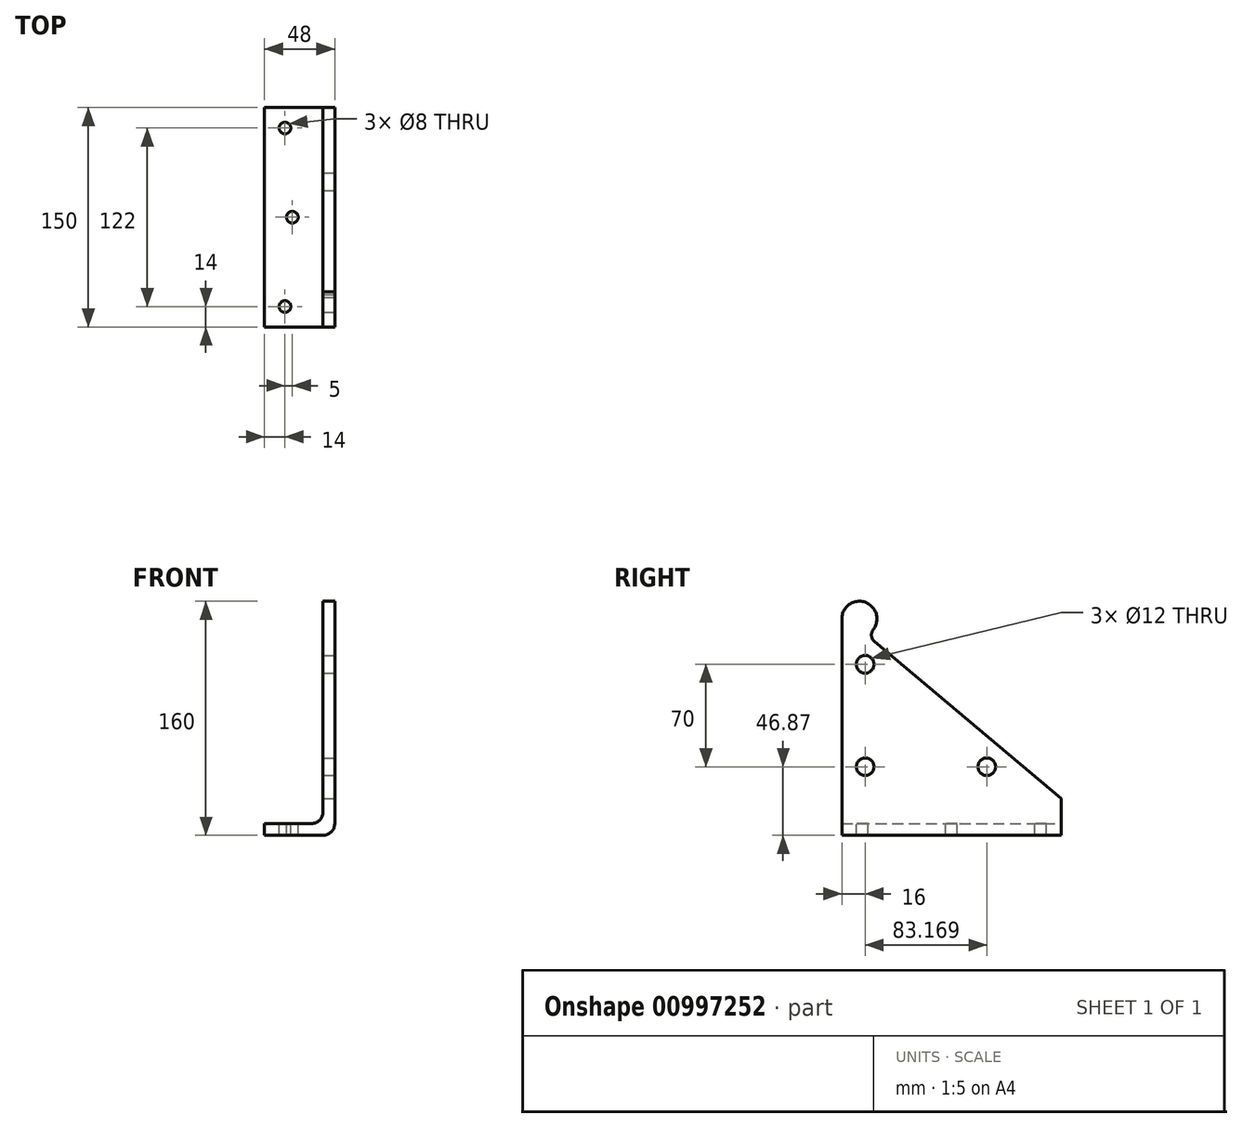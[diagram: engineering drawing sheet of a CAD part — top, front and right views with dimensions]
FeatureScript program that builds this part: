
annotation { "Feature Type Name" : "Feature", "Feature Type Description" : "" }
export const myFeature = defineFeature(function(context is Context, id is Id, definition is map)
    precondition{}
    {
        {
            var Q0;
            Q0=qCreatedBy(makeId("Front.planeOp"),FACE);
            var sketch = newSketch(context, id + "F0", { "sketchPlane" : qUnion([Q0])});
            skLineSegment(sketch, "E0", {"start": v(-4, 80) * mm, "end": v(-4, -72) * mm});
            skLineSegment(sketch, "E1", {"start": v(4, -80) * mm, "end": v(4, 80) * mm});
            skLineSegment(sketch, "E2", {"start": v(4, 80) * mm, "end": v(-4, 80) * mm});
            skLineSegment(sketch, "E3", {"start": v(4, -80) * mm, "end": v(-44, -80) * mm});
            skLineSegment(sketch, "E4", {"start": v(-44, -80) * mm, "end": v(-44, -72) * mm});
            skLineSegment(sketch, "E5", {"start": v(-44, -72) * mm, "end": v(-4, -72) * mm});
            skSolve(sketch);
        }
        {
            var Q0;
            Q0=qSketchRegion(id+"F0",true);
            extrude(context, id + "F1", {"entities" : qUnion([Q0]), "endBound" : BoundingType.SYMMETRIC, "depth" : 150 * mm, "offsetDistance" : 25 * mm});
        }
        {
            var Q0;
            Q0=makeQuery(id+"F1.opExtrude","SWEPT_EDGE",EDGE,{"disambiguationData":[OSD([sQuery(id+"F0.wireOp",EDGE,"E0"),sQuery(id+"F0.wireOp",EDGE,"E5")])]});
            var Q1;
            Q1=makeQuery(id+"F1.opExtrude","SWEPT_EDGE",EDGE,{"disambiguationData":[OSD([sQuery(id+"F0.wireOp",EDGE,"E1"),sQuery(id+"F0.wireOp",EDGE,"E3")])]});
            fillet(context, id + "F2", {"entities" : qUnion([Q0, Q1]), "radius" : 8 * mm, "tangentPropagation" : true, "allowEdgeOverflow" : false});
        }
        {
            var Q0;
            Q0=makeQuery(id+"F1.opExtrude","SWEPT_FACE",FACE,{"disambiguationData":[OSD([sQuery(id+"F0.wireOp",EDGE,"E1")])]});
            var sketch = newSketch(context, id + "F3", { "sketchPlane" : qUnion([Q0])});
            skCircle(sketch, "E6", {"center": v(-63, 68) * mm, "radius": 12 * mm});
            skArc(sketch, "E7", {"start": v(-53.5, 60.67) * mm, "mid": v(-54.72, 56.36) * mm, "end": v(-52.62, 52.4) * mm});
            skLineSegment(sketch, "E8", {"start": v(75, -55) * mm, "end": v(-52.62, 52.4) * mm});
            skLineSegment(sketch, "E9", {"start": v(-63, 80) * mm, "end": v(75, 80) * mm});
            skLineSegment(sketch, "E10", {"start": v(75, 80) * mm, "end": v(75, -55) * mm});
            skCircle(sketch, "E11", {"center": v(-59, 36.87) * mm, "radius": 6 * mm});
            skCircle(sketch, "E12", {"center": v(-59, -33.13) * mm, "radius": 6 * mm});
            skCircle(sketch, "E13", {"center": v(24.17, -33.13) * mm, "radius": 6 * mm});
            skSolve(sketch);
        }
        {
            var Q0;
            {var subQ1=sQuery(id+"F3.wireOp",EDGE,"E7");Q0=makeQuery(id+"F3.imprint","IMPRINT",FACE,{"disambiguationData":[TD([[makeQuery(id+"F3.imprint","IMPRINT",EDGE,{"derivedFrom":subQ1}),1.0]])]});}
            var Q1;
            {var subQ0=sQuery(id+"F3.wireOp",EDGE,"E6");var subQ1=sQuery(id+"F0.wireOp",EDGE,"E1");var subQ4=makeQuery(id+"F1.opExtrude","CAP_EDGE",EDGE,{"disambiguationData":[OSD([subQ1])],"isStart":false});var subQ5=makeQuery(id+"F3.imprint","INTERSECT",VERTEX,{"derivedFrom":[subQ4,subQ0]});Q1=makeQuery(id+"F3.imprint","IMPRINT",FACE,{"disambiguationData":[TD([[makeQuery(id+"F3.imprint","IMPRINT",EDGE,{"disambiguationData":[TD([[subQ5,-1.0]])],"derivedFrom":subQ4}),-1.0]])]});}
            var Q2;
            Q2=makeQuery(id+"F3.imprint","IMPRINT",FACE,{"disambiguationData":[TD([[makeQuery(id+"F3.imprint","IMPRINT",EDGE,{"derivedFrom":sQuery(id+"F3.wireOp",EDGE,"E11")}),1.0]])]});
            var Q3;
            Q3=makeQuery(id+"F3.imprint","IMPRINT",FACE,{"disambiguationData":[TD([[makeQuery(id+"F3.imprint","IMPRINT",EDGE,{"derivedFrom":sQuery(id+"F3.wireOp",EDGE,"E12")}),1.0]])]});
            var Q4;
            Q4=makeQuery(id+"F3.imprint","IMPRINT",FACE,{"disambiguationData":[TD([[makeQuery(id+"F3.imprint","IMPRINT",EDGE,{"derivedFrom":sQuery(id+"F3.wireOp",EDGE,"E13")}),1.0]])]});
            extrude(context, id + "F4", {"entities" : qUnion([Q0, Q1, Q2, Q3, Q4]), "operationType" : NewBodyOperationType.REMOVE, "endBound" : BoundingType.THROUGH_ALL, "oppositeDirection" : true, "depth" : 25 * mm, "offsetDistance" : 25 * mm});
        }
        {
            var Q0;
            Q0=qCreatedBy(makeId("Top.planeOp"),FACE);
            var sketch = newSketch(context, id + "F5", { "sketchPlane" : qUnion([Q0])});
            skCircle(sketch, "E14", {"center": v(-30, -61) * mm, "radius": 4 * mm});
            skCircle(sketch, "E15", {"center": v(-25, 0) * mm, "radius": 4 * mm});
            skCircle(sketch, "E16", {"center": v(-30, 61) * mm, "radius": 4 * mm});
            skSolve(sketch);
        }
        {
            var Q0;
            Q0=qSketchRegion(id+"F5",true);
            extrude(context, id + "F6", {"entities" : qUnion([Q0]), "operationType" : NewBodyOperationType.REMOVE, "endBound" : BoundingType.THROUGH_ALL, "oppositeDirection" : true, "depth" : 0 * mm, "offsetDistance" : 25 * mm});
        }
    });
